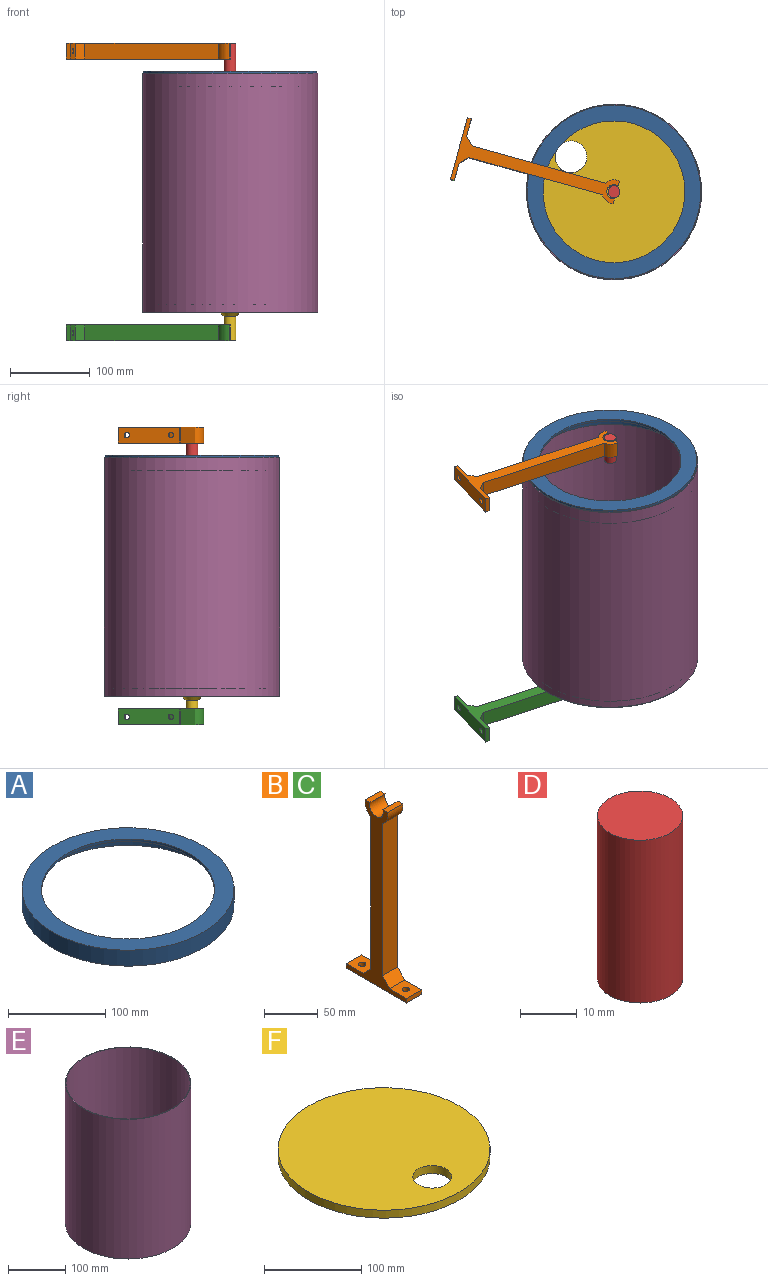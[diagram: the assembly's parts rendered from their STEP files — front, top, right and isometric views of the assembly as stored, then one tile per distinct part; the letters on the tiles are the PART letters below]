
ASSEMBLY  parts=6 mates=9
PART A: 6 faces, bbox 218x218x20 mm
  f0: plane 218x218mm, normal (0,0,1), area 12440.7mm2, adj f1,f5
  f1: cylinder r=109mm len=218mm, axis (0,0,1), area 13697.3mm2, adj f0,f2
  f2: plane 218x218mm, normal (0,0,-1), area 2026.3mm2, adj f1,f3
  f3: cylinder r=106mm len=212mm, axis (0,0,1), area 11322.3mm2, adj f2,f4
  f4: plane 212x212mm, normal (0,0,-1), area 10414.4mm2, adj f3,f5
  f5: cylinder r=89mm len=178mm, axis (0,0,1), area 1677.6mm2, adj f0,f4
PART B: 18 faces, bbox 20x80x205 mm
  f0: plane 20x6.21mm, normal (0,0,1), area 124.1mm2, adj f1,f11,f12,f13
  f1: cylinder r=15mm len=20mm, axis (-1,0,0), area 373.7mm2, adj f0,f2,f12,f13
  f2: plane 174.05x20mm, normal (0,-1,0), area 3481mm2, adj f1,f12,f13,f14
  f3: plane 22.5x20mm, normal (0,0,1), area 411.5mm2, adj f4,f12,f13,f14,f17
  f4: plane 20x5mm, normal (0,-1,0), area 100mm2, adj f3,f5,f12,f13
  f5: plane 80x20mm, normal (0,0,-1), area 1523mm2, adj f4,f6,f12,f13,f16,f17
  f6: plane 20x5mm, normal (0,1,0), area 100mm2, adj f5,f7,f12,f13
  f7: plane 22.5x20mm, normal (0,0,1), area 411.5mm2, adj f6,f12,f13,f15,f16
  f8: plane 174.05x20mm, normal (0,1,0), area 3481mm2, adj f9,f12,f13,f15
  f9: cylinder r=15mm len=20mm, axis (-1,0,0), area 373.7mm2, adj f8,f10,f12,f13
  f10: plane 20x6.21mm, normal (0,0,1), area 124.1mm2, adj f9,f11,f12,f13
  f11: cylinder r=9mm len=20mm, axis (-1,0,0), area 686mm2, adj f0,f10,f12,f13
  f12: plane 205x80mm, normal (1,0,0), area 3502.5mm2, adj f0,f1,f2,f3,f4,f5,f6,f7
  f13: plane 205x80mm, normal (-1,0,0), area 3502.5mm2, adj f0,f1,f2,f3,f4,f5,f6,f7
  f14: plane 20x10mm, normal (0,-0.71,0.71), area 282.8mm2, adj f2,f3,f12,f13
  f15: plane 20x10mm, normal (0,0.71,0.71), area 282.8mm2, adj f7,f8,f12,f13
  f16: cylinder r=3.5mm len=7mm, axis (0,0,1), area 110mm2, adj f5,f7
  f17: cylinder r=3.5mm len=7mm, axis (0,0,1), area 110mm2, adj f3,f5
PART C: same geometry as B
PART D: 5 faces, bbox 15x15x35 mm
  f0: cylinder r=7.5mm len=35mm, axis (0,0,-1), area 1649.3mm2, adj f1,f2
  f1: plane 15x15mm, normal (0,0,1), area 176.7mm2, adj f0
  f2: plane 15x15mm, normal (0,0,-1), area 162.9mm2, adj f0,f4
  f3: cone r=0mm half-angle=59deg, axis (0,0,-1), area 16.2mm2, adj f4
  f4: cylinder r=2.1mm len=15mm, axis (0,0,-1), area 197.9mm2, adj f2,f3
PART E: 4 faces, bbox 220x220x300 mm
  f0: cylinder r=109mm len=300mm, axis (0,0,-1), area 205460.2mm2, adj f2,f3
  f1: cylinder r=110mm len=300mm, axis (0,0,-1), area 207345.1mm2, adj f2,f3
  f2: plane 220x220mm, normal (0,0,1), area 688mm2, adj f0,f1
  f3: plane 220x220mm, normal (0,0,-1), area 688mm2, adj f0,f1
PART F: 7 faces, bbox 218x218x45 mm
  f0: cylinder r=109mm len=218mm, axis (0,0,-1), area 6848.7mm2, adj f1,f2
  f1: plane 218x218mm, normal (0,0,1), area 36068.6mm2, adj f0,f3
  f2: plane 218x218mm, normal (0,0,-1), area 35577.8mm2, adj f0,f3,f6
  f3: cylinder r=20mm len=40mm, axis (0,0,-1), area 1256.6mm2, adj f1,f2
  f4: cylinder r=7.5mm len=30mm, axis (0,0,1), area 1413.7mm2, adj f5,f6
  f5: plane 15x15mm, normal (0,0,-1), area 176.7mm2, adj f4
  f6: cone r=7.5mm half-angle=45deg, axis (0,0,1), area 444.3mm2, adj f2,f4
PLACE A rot(axis=(0,0,1),8.8deg) t=(-27.84,-63.22,75.33)mm
PLACE B rot(axis=(0.13,0.98,-0.13),91.1deg) t=(-27.84,-63.22,110.33)mm
PLACE C rot(axis=(0.13,0.98,-0.13),91.1deg) t=(-27.84,-63.22,-243.37)mm fixed
PLACE D rot(axis=(0,0,1),82.2deg) t=(-27.84,-63.22,75.33)mm
PLACE E rot(axis=(0,0,1),20.9deg) t=(-27.84,-63.22,-227.53)mm
PLACE F rot(axis=(0,0,-1),129.5deg) t=(-27.84,-63.22,-228.37)mm
MATE planar D.f0 <-> B.f13  axis (0,0,1) through (-27.84,-63.22,110.33)mm
MATE planar D.f0 <-> A.f1  axis (0,0,-1) through (-27.84,-63.22,75.33)mm
MATE cylindrical B.f11 <-> D.f0  axis (0,0,1) through (-27.84,-63.22,110.33)mm
MATE cylindrical D.f0 <-> A.f1  axis (0,0,-1) through (-27.84,-63.22,92.83)mm
MATE planar C.f5 <-> B.f5  axis (-0.96,0.27,0) through (-222.45,-8.93,-253.37)mm
MATE planar C.f12 <-> F.f4  axis (0,0,-1) through (-42.36,-66.95,-263.37)mm
MATE cylindrical A.f1 <-> E.f1  axis (0,0,1) through (-27.84,-63.22,75.33)mm
MATE cylindrical F.f4 <-> C.f11  axis (0,0,1) through (-27.84,-63.22,-248.37)mm
MATE cylindrical F.f0 <-> E.f1  axis (0,0,-1) through (-27.84,-63.22,-228.37)mm
